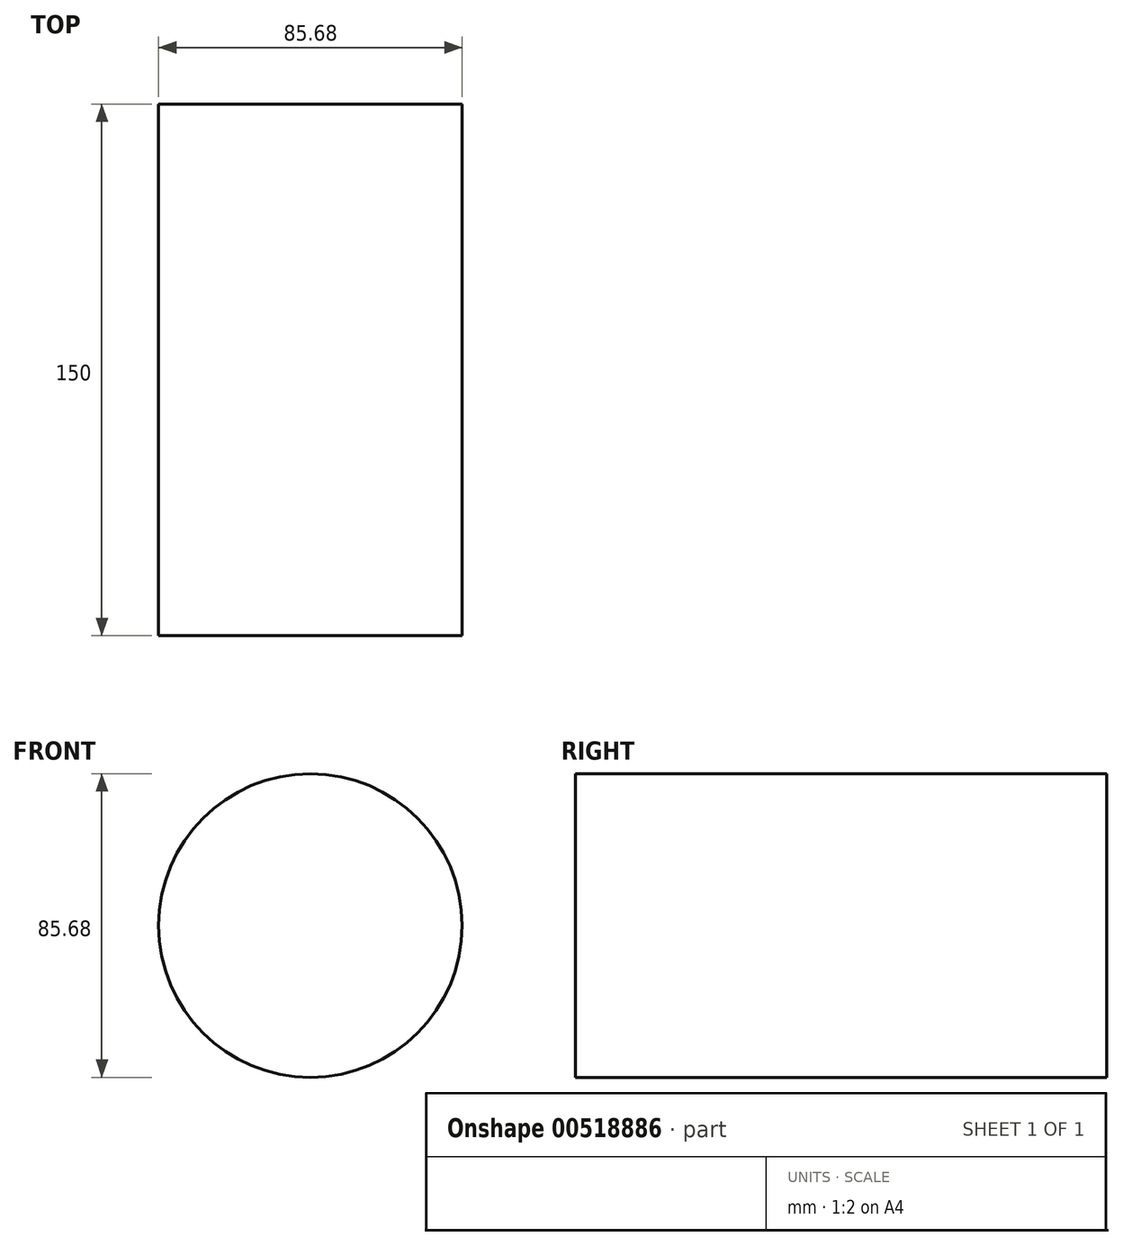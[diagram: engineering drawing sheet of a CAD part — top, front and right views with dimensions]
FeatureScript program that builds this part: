
annotation { "Feature Type Name" : "Feature", "Feature Type Description" : "" }
export const myFeature = defineFeature(function(context is Context, id is Id, definition is map)
    precondition{}
    {
        {
            var Q0;
            Q0=qCreatedBy(makeId("Front.planeOp"),FACE);
            var sketch = newSketch(context, id + "F0", { "sketchPlane" : qUnion([Q0])});
            skCircle(sketch, "E0", {"center": v(0, 0) * mm, "radius": 42.84 * mm});
            skSolve(sketch);
        }
        {
            var Q0;
            Q0=makeQuery(id+"F0.imprint","IMPRINT",FACE,{"disambiguationData":[TD([[makeQuery(id+"F0.imprint","IMPRINT",EDGE,{"derivedFrom":sQuery(id+"F0.wireOp",EDGE,"E0")}),1.0]])]});
            extrude(context, id + "F1", {"entities" : qUnion([Q0]), "depth" : 150 * mm, "offsetDistance" : 25.4 * mm});
        }
    });
